# Revit family: TYCO-FPP-FireClass-FC410TSM DOOR CONTROL MODULE
name_source: partatom
category: Electrical Fixtures
revit_build: Autodesk Revit 2014 (Build: 20130308_1515(x64)
units: mm (PartAtom-declared; Revit-internal decimal feet)

## types (1)
- TYCO-FPP-FireClass-FC410TSM DOOR CONTROL MODULE
    Approvals = VdS EN 54-17 & EN 54-18 standards
    Description = FC410TSM DOOR CONTROL MODULE
    Front Cover = Yes
    Keynote = The new FC410TSM Door Control Module is designed to close a door in case of fire or fault event
    Length = 60 mm
    Loop Voltage = 24 V
    Manufacturer = Tyco
    Model = FireClass- 555.800.769
    Operating temperature = -25 to +70 °C
    PCB = PCB
    Rear Cover = Yes
    Relative Humidity = 95% (non condensing)
    ST1 = ST1
    STT = STT
    Storage Temperature = -40 a +80 °C
    Type Comments = Its monitored input provides the possibility to check if the door is really closed
    URL = http://www.bentelsecurity.com
    Width = 80 mm

## geometry (parser evidence)
native form markers: Sweep x8
no freeform markers — native parametric forms only
